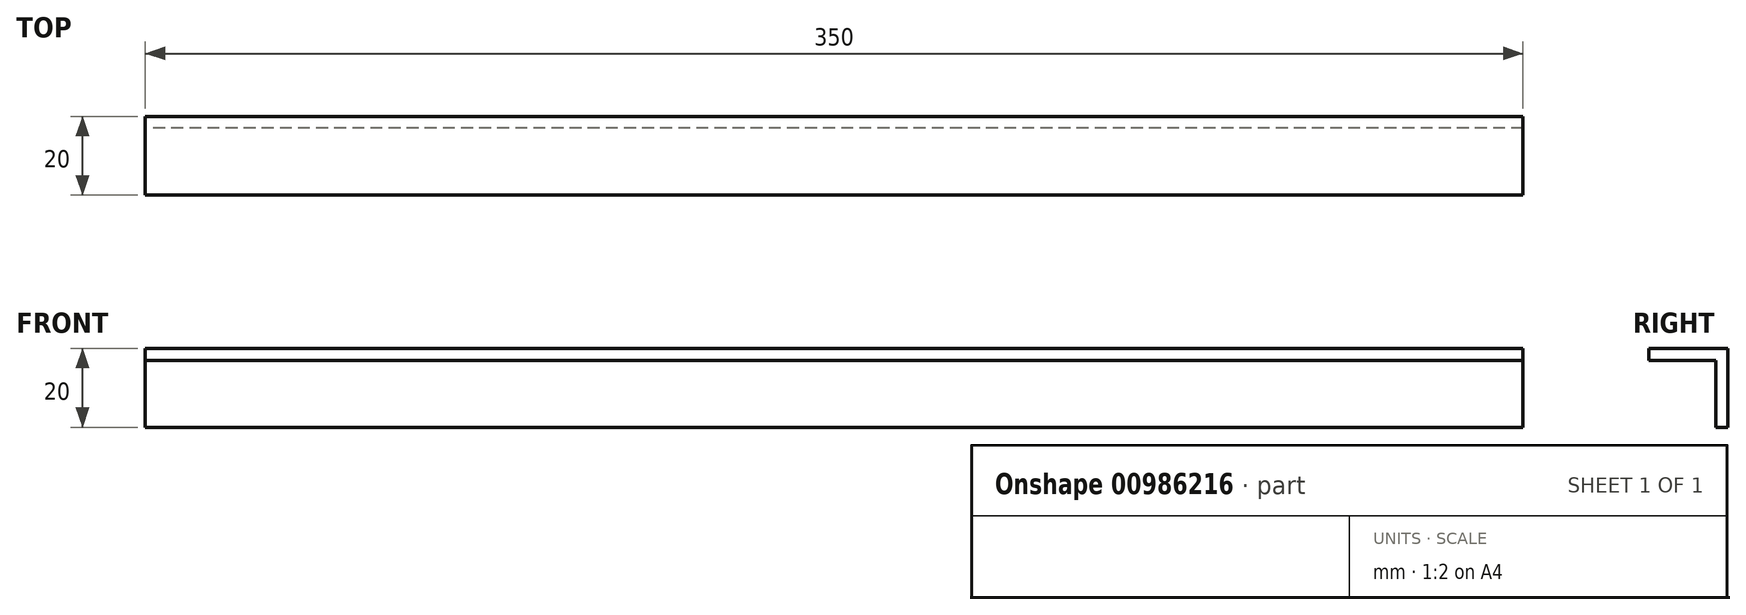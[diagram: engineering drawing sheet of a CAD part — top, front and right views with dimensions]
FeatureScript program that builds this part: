
annotation { "Feature Type Name" : "Feature", "Feature Type Description" : "" }
export const myFeature = defineFeature(function(context is Context, id is Id, definition is map)
    precondition{}
    {
        {
            var Q0;
            Q0=qCreatedBy(makeId("Right.planeOp"),FACE);
            var sketch = newSketch(context, id + "F0", { "sketchPlane" : qUnion([Q0])});
            skLineSegment(sketch, "E0", {"start": v(0, 0) * mm, "end": v(20, 0) * mm});
            skLineSegment(sketch, "E1", {"start": v(20, 0) * mm, "end": v(20, -20) * mm});
            skLineSegment(sketch, "E2", {"start": v(20, -20) * mm, "end": v(17, -20) * mm});
            skLineSegment(sketch, "E3", {"start": v(17, -20) * mm, "end": v(17, -3) * mm});
            skLineSegment(sketch, "E4", {"start": v(17, -3) * mm, "end": v(0, -3) * mm});
            skLineSegment(sketch, "E5", {"start": v(0, -3) * mm, "end": v(0, 0) * mm});
            skSolve(sketch);
        }
        {
            var Q0;
            Q0=makeQuery(id+"F0.imprint","IMPRINT",FACE,{"disambiguationData":[TD([[makeQuery(id+"F0.imprint","IMPRINT",EDGE,{"derivedFrom":sQuery(id+"F0.wireOp",EDGE,"E0")}),-1.0]])]});
            extrude(context, id + "F1", {"entities" : qUnion([Q0]), "depth" : 350 * mm, "offsetDistance" : 25 * mm});
        }
    });
